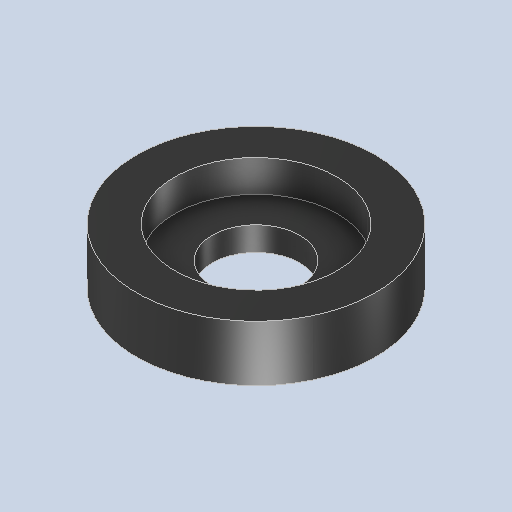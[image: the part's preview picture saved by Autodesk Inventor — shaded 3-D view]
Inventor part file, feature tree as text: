
AUTODESK INVENTOR PART (.ipt)
format: ipt  version: 2024.2 (Build 282272000, 272)  size: 122,368 bytes
history: native  units: mm
features: revolve x1, sketch x1
ambient origin geometry x8: Origin, YZ Plane, XZ Plane, XY Plane, X Axis, Y Axis, Z Axis, Center Point
bodies: Solid1 (feature_tree)
feature tree (2):
  revolve  "Revolution1"  [1 undecoded]
  sketch  "Sketch1"  dims[d0=15.0mm d1=10.2mm d2=5.5mm d3=2.0mm d4=3.5mm d5=90.0deg]
note: 1 required parameter value undecoded (feature->parameter linkage not recoverable at this tier; creation-order binding heuristic only, values carry confidence <= 0.55)
